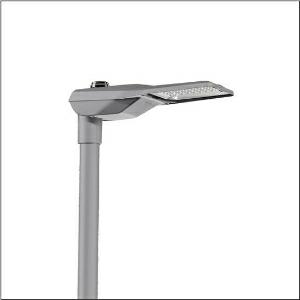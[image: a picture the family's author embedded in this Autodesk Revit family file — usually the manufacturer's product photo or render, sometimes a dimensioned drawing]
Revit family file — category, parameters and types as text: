
# Revit family: streetlight_sl_21_mini___p1_0a_5xe6a37n08hb_d726
name_source: partatom
category: Lighting Fixtures
units: mm (PartAtom-declared; Revit-internal decimal feet)

## family parameters
Cut with Voids When Loaded = No
Host = Face
Light Source = No
Part Type = Normal
Room Calculation Point = No
Round Connector Dimension = Use Diameter
Shared = No

## types (1)
- --- (1 x LED, 9040 lm, 66 W, 3000K)
    Apparent Load = 66 VA
    CIE Flux Codes = 21 50 90 100 100
    Color Rendering = 70
    Color Temperature = 3000K
    Default Elevation = 1800 mm
    Description = Streetlight SL 21 mini, mast luminaire, primary light control with lens, of PMMA, primary optical cover: cover, of toughened safety glass, transparent, light distribution: P1.0a, light emission: direct distribution, primary light characteristic: asymmetric, installation type: side-entry, LED, 3G 1.5mm², High Power LED, rated luminous flux: 9.040lm, luminous efficacy: 137lm/W, light colour: 730, colour temperature: 3000K, control gear: NEMA (7pin), control: overheat protection, pre-setting: linear dimming characteristic, constant luminous flux control, time-dependent luminous flux control, flexible luminous flux parameterisation, mains connection: 230..240V, AC, 50/60Hz, connection cable pre-assembled, cable length: 8,5m, wiring characteristics: H07RN-F, start of lifetime: 66W, end of service life: 69W, reduction: 30W, luminaire housing, of diecast aluminium (EN AC-44300), powder-coated, Siteco® metallic grey (DB 702S), corrosivity category C5 mid according to DIN EN ISO 12944, multi-level sealing system, sealing non-destructively replaceable, inclination adjustable: 0°, 5°, 10°, 15°, length: 628mm, width: 235mm, height: 110mm, spigot size: 42mm (side-entry), mounting height: 4..8m, protection rating (complete): IP66, insulation class (complete): insulation class I (protective earthing), certification: CE, ENEC, ENEC+, VDE, impact resistance: IK10, permissible operating ambient temperature for outdoor applications: -40..+50°C, standard-compliant lighting for roads and squares, packaging unit: 1 piece

Light Distribution: P1.0a
    Height = 110 mm
    Lamp = 1 x LED
    Lamp Light Flux = 9040 lm
    Lamp Power = 66 W
    Lamp count = 1
    Length = 625 mm
    Luminous efficacy = 137 lm/W
    Manufacturer = Siteco
    ModVariant = No
    Model = 5XE6A37N08HB
    Number of Poles = 1
    OnlyDefault = Yes
    Power Factor = 1
    Product Name = Streetlight SL 21 mini | P1.0a
    Product group = mast luminaire | pylon top
    ProductGroupID = 6100
    Protection Class = Protection class I
    Protection Degree = IP 66
    RLX_Detail_Level = 1
    RLX_Emergency_Light_Flux = 0 lm
    RLX_Emergency_Type = 0
    RLX_Emergency_Type_DB = No
    RlxData = <blob elided: 37445 chars, md5=5ab62844>
    Socket = socket
    Standby Power = 0 W
    System Light Flux = 9040 lm
    System Power = 66 W
    Type Comments = factory setting: luminous flux: 100 % | dim-lin: 254 | 670 mA
    Type Image = l_1294379.jpg
    URL = http://relux.com
    VarID = @adj_134678
    Voltage = 0 V
    Weight = 0.00 kg
    Width = 234 mm

## geometry (parser evidence)
native form markers: Blend x4, Sweep x10
no freeform markers — native parametric forms only
